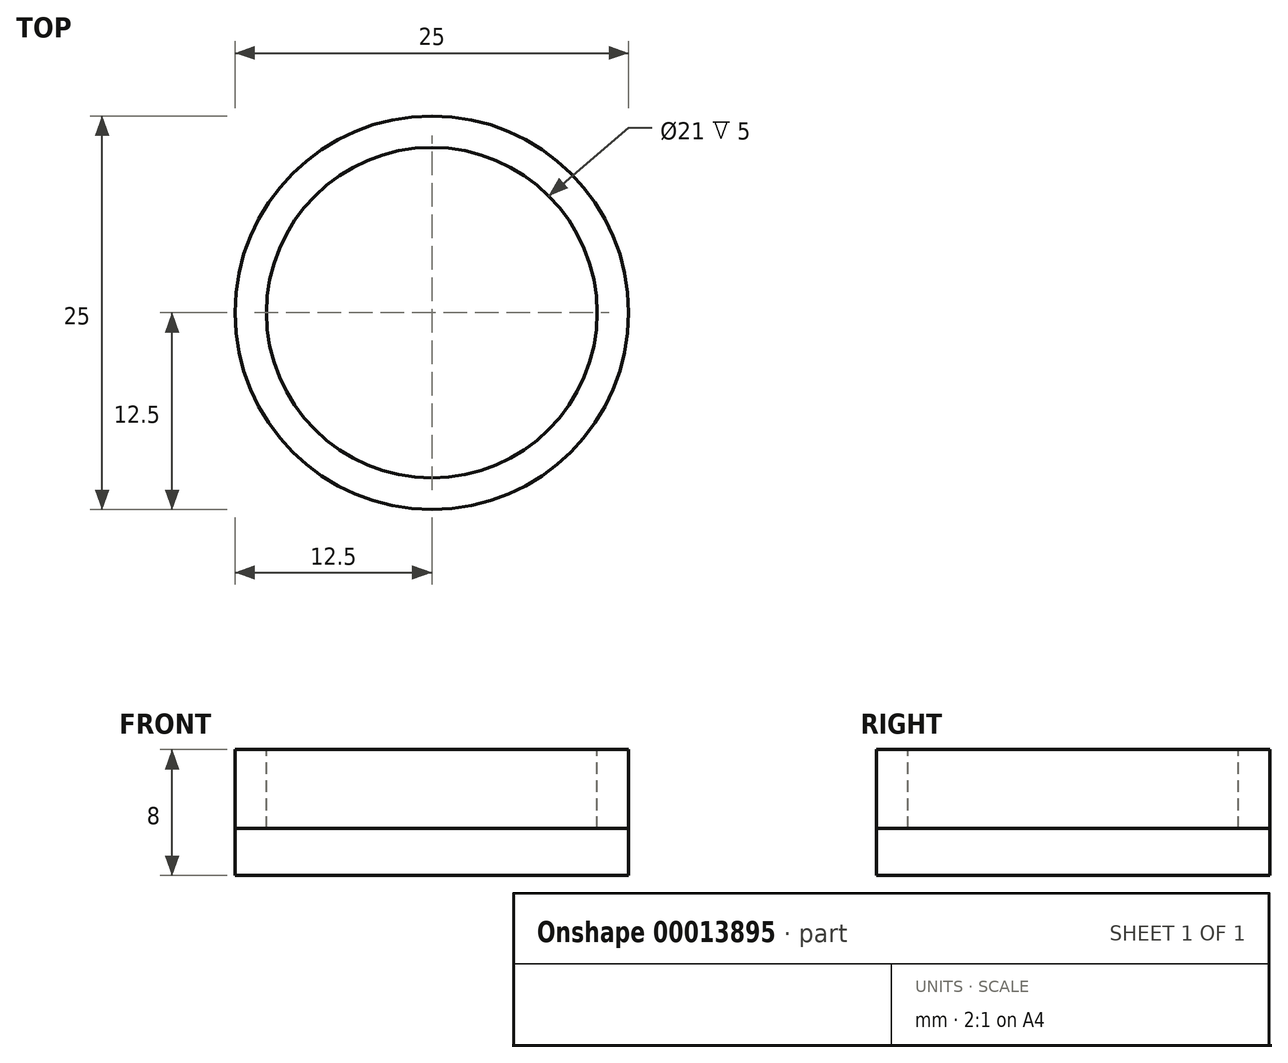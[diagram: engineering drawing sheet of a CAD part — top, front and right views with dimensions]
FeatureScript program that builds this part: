
annotation { "Feature Type Name" : "Feature", "Feature Type Description" : "" }
export const myFeature = defineFeature(function(context is Context, id is Id, definition is map)
    precondition{}
    {
        {
            var Q0;
            Q0=qCreatedBy(makeId("Top.planeOp"),FACE);
            var sketch = newSketch(context, id + "F0", { "sketchPlane" : qUnion([Q0])});
            skCircle(sketch, "E0", {"center": v(0, 0) * mm, "radius": 12.5 * mm});
            skSolve(sketch);
        }
        {
            var Q0;
            Q0 = qSketchRegion(id + "F0", true);
            extrude(context, id + "F1", {"entities" : qUnion([Q0]), "depth" : 3 * mm});
        }
        {
            var Q0;
            Q0=makeQuery(id+"F1.opExtrude","CAP_FACE",FACE,{"disambiguationData":[OSD([sQuery(id+"F0.wireOp",EDGE,"E0")])],"isStart":false});
            var sketch = newSketch(context, id + "F2", { "sketchPlane" : qUnion([Q0])});
            skCircle(sketch, "E1", {"center": v(0, 0) * mm, "radius": 10.5 * mm});
            skSolve(sketch);
        }
        {
            var Q0;
            Q0=makeQuery(id+"F2.imprint","IMPRINT",FACE,{"disambiguationData":[TD([[makeQuery(id+"F2.imprint","IMPRINT",EDGE,{"derivedFrom":sQuery(id+"F2.wireOp",EDGE,"E1")}),1.0]])]});
            extrude(context, id + "F3", {"entities" : qUnion([Q0]), "operationType" : NewBodyOperationType.ADD, "depth" : 5 * mm});
        }
        {
            var Q0;
            Q0=makeQuery(id+"F3.opExtrude","CAP_FACE",FACE,{"disambiguationData":[OSD([sQuery(id+"F2.wireOp",EDGE,"E1")])],"isStart":false});
            var sketch = newSketch(context, id + "F4", { "sketchPlane" : qUnion([Q0])});
            skCircle(sketch, "E2", {"center": v(0, 0) * mm, "radius": 12.5 * mm});
            skSolve(sketch);
        }
        {
            var Q0;
            Q0=makeQuery(id+"F4.imprint","IMPRINT",FACE,{"disambiguationData":[TD([[makeQuery(id+"F4.imprint","IMPRINT",EDGE,{"derivedFrom":sQuery(id+"F4.wireOp",EDGE,"E2")}),1.0]])]});
            var Q1;
            Q1=makeQuery(id+"F1.opExtrude","CAP_FACE",FACE,{"disambiguationData":[OSD([sQuery(id+"F0.wireOp",EDGE,"E0")])],"isStart":false});
            extrude(context, id + "F5", {"entities" : qUnion([Q0]), "endBound" : BoundingType.UP_TO_SURFACE, "oppositeDirection" : true, "endBoundEntityFace" : qUnion([Q1]), "depth" : 3 * mm});
        }
    });
